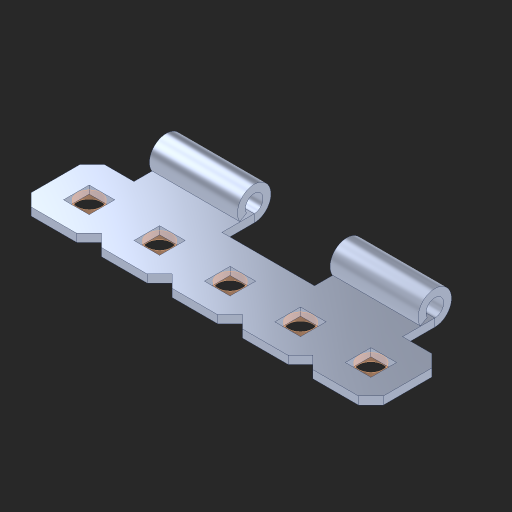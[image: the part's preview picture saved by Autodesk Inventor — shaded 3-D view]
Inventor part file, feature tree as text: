
AUTODESK INVENTOR PART (.ipt)
format: ipt  version: 2023 (Build 270158000, 158)  size: 210,432 bytes
history: native  units: in
note: dims shown in document units (in); Inventor stores cm internally (conversion verified against a paired STEP export)
features: other x7, extrude x5, pattern_linear x1, imported_body x1, sketch x1
ambient origin geometry x8: Origin, YZ Plane, XZ Plane, XY Plane, X Axis, Y Axis, Z Axis, Center Point
bodies: Body1 (feature_tree), Body2 (feature_tree), Body3 (feature_tree), Body4 (feature_tree), Body5 (feature_tree), Body6 (feature_tree)
feature tree (15):
  other  "Cut-Extrude3"
  other  "Bottom"
  pattern_linear  "Rectangular Pattern1"  Count1=5 Spacing1=0.5in
  imported_body  "Base1"
  sketch  "Sketch1"  dims[d15=0.046in d16=0.0in d17=1.9685in d19=0.5in d30=0.172in]
  other  "Srf1"
  other  "Srf2"
  other  "Srf3"
  other  "Srf4"
  other  "Srf5"
  extrude  "ExtrusionSrf1"  Depth=0.5in
  extrude  "ExtrusionSrf2"  [1 undecoded]
  extrude  "ExtrusionSrf3"  [1 undecoded]
  extrude  "ExtrusionSrf4"  [1 undecoded]
  extrude  "ExtrusionSrf5"  [1 undecoded]
note: 4 required parameter values undecoded (feature->parameter linkage not recoverable at this tier; creation-order binding heuristic only, values carry confidence <= 0.55)
